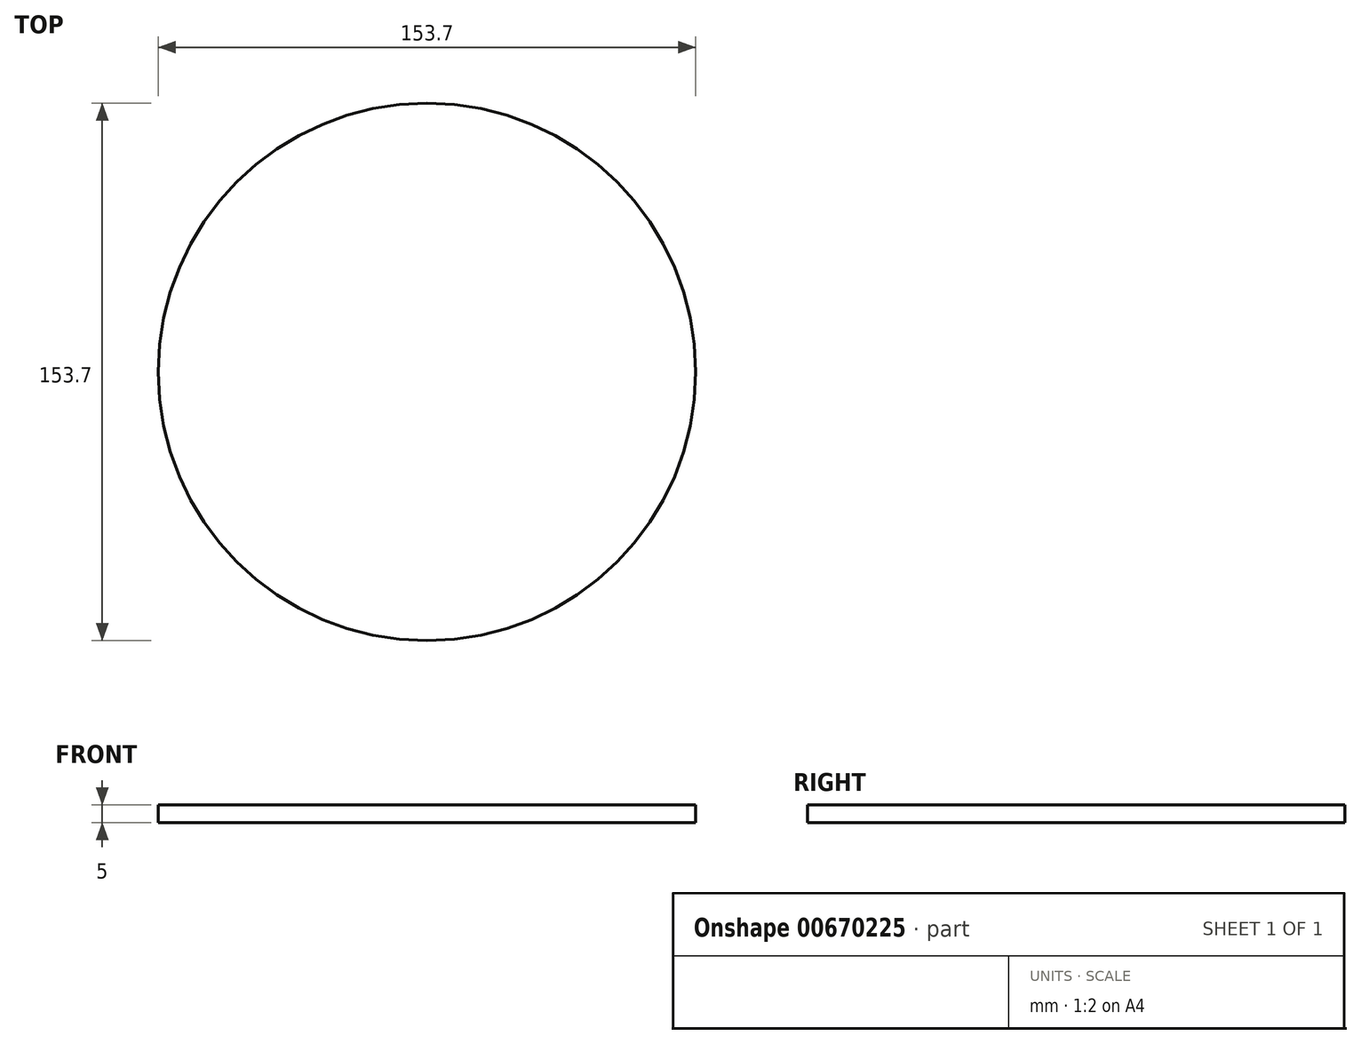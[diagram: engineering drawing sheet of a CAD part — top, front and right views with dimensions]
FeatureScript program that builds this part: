
annotation { "Feature Type Name" : "Feature", "Feature Type Description" : "" }
export const myFeature = defineFeature(function(context is Context, id is Id, definition is map)
    precondition{}
    {
        {
            var Q0;
            Q0=qCreatedBy(makeId("Top.planeOp"),FACE);
            var sketch = newSketch(context, id + "F0", { "sketchPlane" : qUnion([Q0])});
            skCircle(sketch, "E0", {"center": v(0, 0) * mm, "radius": 76.85 * mm});
            skSolve(sketch);
        }
        {
            var Q0;
            Q0=makeQuery(id+"F0.imprint","IMPRINT",FACE,{"disambiguationData":[TD([[makeQuery(id+"F0.imprint","IMPRINT",EDGE,{"derivedFrom":sQuery(id+"F0.wireOp",EDGE,"E0")}),1.0]])]});
            extrude(context, id + "F1", {"entities" : qUnion([Q0]), "depth" : 5 * mm, "offsetDistance" : 25.4 * mm});
        }
    });
